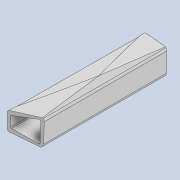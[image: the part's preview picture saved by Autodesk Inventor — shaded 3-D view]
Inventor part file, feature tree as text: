
AUTODESK INVENTOR PART (.ipt)
format: ipt  version: 2020.4 (Build 244396010, 396A)  size: 286,208 bytes
history: native  units: in
note: dims shown in document units (in); Inventor stores cm internally (conversion verified against a paired STEP export)
features: plane x12, other x9, surface_op x9, sketch x3, loft x2, boolean_combine x2, mirror x2, direct_edit x2, fillet x1
ambient origin geometry x8: Origin, YZ Plane, XZ Plane, XY Plane, X Axis, Y Axis, Z Axis, Center Point
bodies: Solid2 (feature_tree), Solid4 (feature_tree), Solid1 (feature_tree)
feature tree (42):
  other  "handle_body_final.ipt"
  other  "MidPlane"
  loft  "FrontLoftFeature"
  other  "FrontProfilePlane"
  sketch  "Sketch9"  dims[d0=0.3937in d1=0.0in d2=90.0deg]
  plane  "Work Plane13"
  plane  "Work Plane14"
  plane  "Work Plane15"
  plane  "Work Plane16"
  boolean_combine  "Combine3"
  surface_op  "Sculpt12"
  surface_op  "Sculpt13"
  surface_op  "Sculpt15"
  surface_op  "Sculpt16"
  loft  "Loft3"
  mirror  "Mirror2"
  mirror  "Mirror3"
  boolean_combine  "Combine6"
  direct_edit  "Direct Edit2"
  surface_op  "Sculpt19"
  surface_op  "Sculpt20"
  surface_op  "Sculpt21"
  direct_edit  "Direct Edit3"
  surface_op  "Sculpt22"
  surface_op  "Sculpt23"
  fillet  "Fillet4"  Radius=0.1181in
  other  "Volumenkörper1::handle_body_final.ipt"
  other  "TaggingFeature1"
  other  "FrontLoftSection1"
  other  "FrontLoftSection2"
  plane  "Work Plane19"
  plane  "Work Plane20"
  plane  "Work Plane21"
  sketch  "Sketch10"  dims[d3=0.0in d4=90.0deg d6=0.1575in d7=0.1181in]
  sketch  "Sketch11"  dims[d8=0.3543in d9=0.3543in d38=120.0deg d41=0.1575in d42=0.3543in d43=0.3543in d44=0.1181in d45=0.0in d46=90.0deg d47=0.0in d48=90.0deg d50=0.1575in]
  plane  "Work Plane27"
  plane  "Work Plane28"
  plane  "Work Plane29"
  plane  "Work Plane30"
  plane  "Work Plane31"
  other  "Delete2"
  other  "Delete3"
